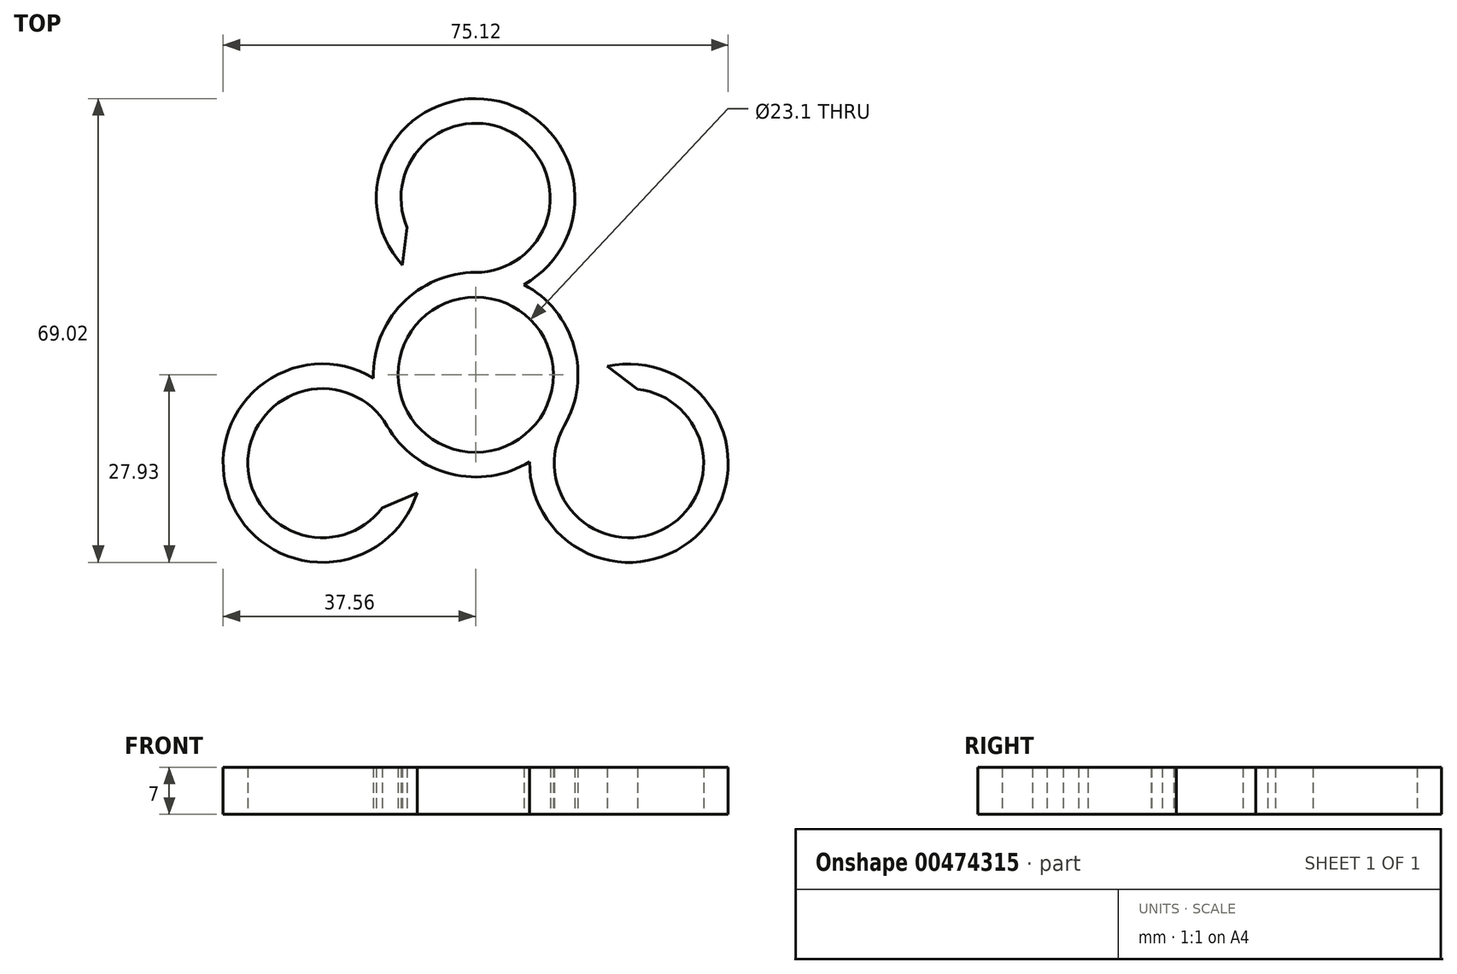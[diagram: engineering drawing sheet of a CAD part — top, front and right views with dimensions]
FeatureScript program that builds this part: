
annotation { "Feature Type Name" : "Feature", "Feature Type Description" : "" }
export const myFeature = defineFeature(function(context is Context, id is Id, definition is map)
    precondition{}
    {
        {
            var Q0;
            Q0=qCreatedBy(makeId("Top.planeOp"),FACE);
            var sketch = newSketch(context, id + "F0", { "sketchPlane" : qUnion([Q0])});
            skCircle(sketch, "E0", {"center": v(0, 0) * mm, "radius": 11.55 * mm});
            skArc(sketch, "E1", {"start": v(0, 15.22) * mm, "mid": v(6.1, 35.6) * mm, "end": v(-10.2, 21.93) * mm});
            skArc(sketch, "E2.1.1", {"start": v(-13.18, -7.61) * mm, "mid": v(-33.87, -12.51) * mm, "end": v(-13.9, -19.8) * mm});
            skArc(sketch, "E2.2.1", {"start": v(13.18, -7.61) * mm, "mid": v(27.77, -23.08) * mm, "end": v(24.09, -2.14) * mm});
            skPoint(sketch, "E3.trimOffspring.end.orphan", {"position": v(15.24, 0.45) * mm});
            skPoint(sketch, "E4.orphan", {"position": v(-7.62, 13.2) * mm});
            skPoint(sketch, "E5.orphan", {"position": v(-15.24, 0) * mm});
            skPoint(sketch, "E6.bottom.end.orphan", {"position": v(15.24, 0) * mm});
            skPoint(sketch, "E6.left.end.orphan", {"position": v(-15.24, 41.1) * mm});
            skPoint(sketch, "E6.top.end.orphan", {"position": v(15.24, 41.09) * mm});
            skPoint(sketch, "E7.trimOffspring.end.orphan", {"position": v(0, 41.1) * mm});
            skPoint(sketch, "E8.start.orphan", {"position": v(0, 11.55) * mm});
            skArc(sketch, "E9", {"start": v(-8.03, -12.93) * mm, "mid": v(0, -15.22) * mm, "end": v(8.03, -12.93) * mm});
            skArc(sketch, "E10", {"start": v(-15.21, -0.48) * mm, "mid": v(-36.6, -18.4) * mm, "end": v(-8.7, -17.6) * mm});
            skArc(sketch, "E11", {"start": v(8.03, -12.93) * mm, "mid": v(34.24, -22.5) * mm, "end": v(19.6, 1.26) * mm});
            skArc(sketch, "E12", {"start": v(7.19, 13.42) * mm, "mid": v(2.36, 40.9) * mm, "end": v(-10.89, 16.34) * mm});
            skArc(sketch, "E13.trimOffspring", {"start": v(15.21, -0.48) * mm, "mid": v(13.18, 7.6) * mm, "end": v(7.19, 13.42) * mm});
            skArc(sketch, "E14.trimOffspring", {"start": v(-7.19, 13.42) * mm, "mid": v(-13.18, 7.6) * mm, "end": v(-15.21, -0.48) * mm});
            skLineSegment(sketch, "E15", {"start": v(-13.9, -19.8) * mm, "end": v(-8.7, -17.6) * mm});
            skArc(sketch, "E16", {"start": v(-8.02, -13.16) * mm, "mid": v(-8.02, -13.05) * mm, "end": v(-8.03, -12.93) * mm});
            skArc(sketch, "E17", {"start": v(-13.18, -7.61) * mm, "mid": v(-3.7, -14.76) * mm, "end": v(8.03, -12.93) * mm});
            skLineSegment(sketch, "E18.1.0", {"start": v(24.09, -2.14) * mm, "end": v(19.6, 1.26) * mm});
            skLineSegment(sketch, "E18.2.0", {"start": v(-10.2, 21.93) * mm, "end": v(-10.89, 16.34) * mm});
            skArc(sketch, "E19.trimOffspring", {"start": v(13.18, -7.6) * mm, "mid": v(14.64, 4.17) * mm, "end": v(7.19, 13.42) * mm});
            skArc(sketch, "E20.trimOffspring", {"start": v(0, 15.22) * mm, "mid": v(-10.93, 10.59) * mm, "end": v(-15.21, -0.48) * mm});
            skSolve(sketch);
        }
        {
            var Q0;
            Q0=makeQuery(id+"F0.imprint","IMPRINT",FACE,{"disambiguationData":[TD([[makeQuery(id+"F0.imprint","IMPRINT",EDGE,{"derivedFrom":sQuery(id+"F0.wireOp",EDGE,"E0")}),-1.0]])]});
            extrude(context, id + "F1", {"entities" : qUnion([Q0]), "depth" : 7 * mm});
        }
    });
